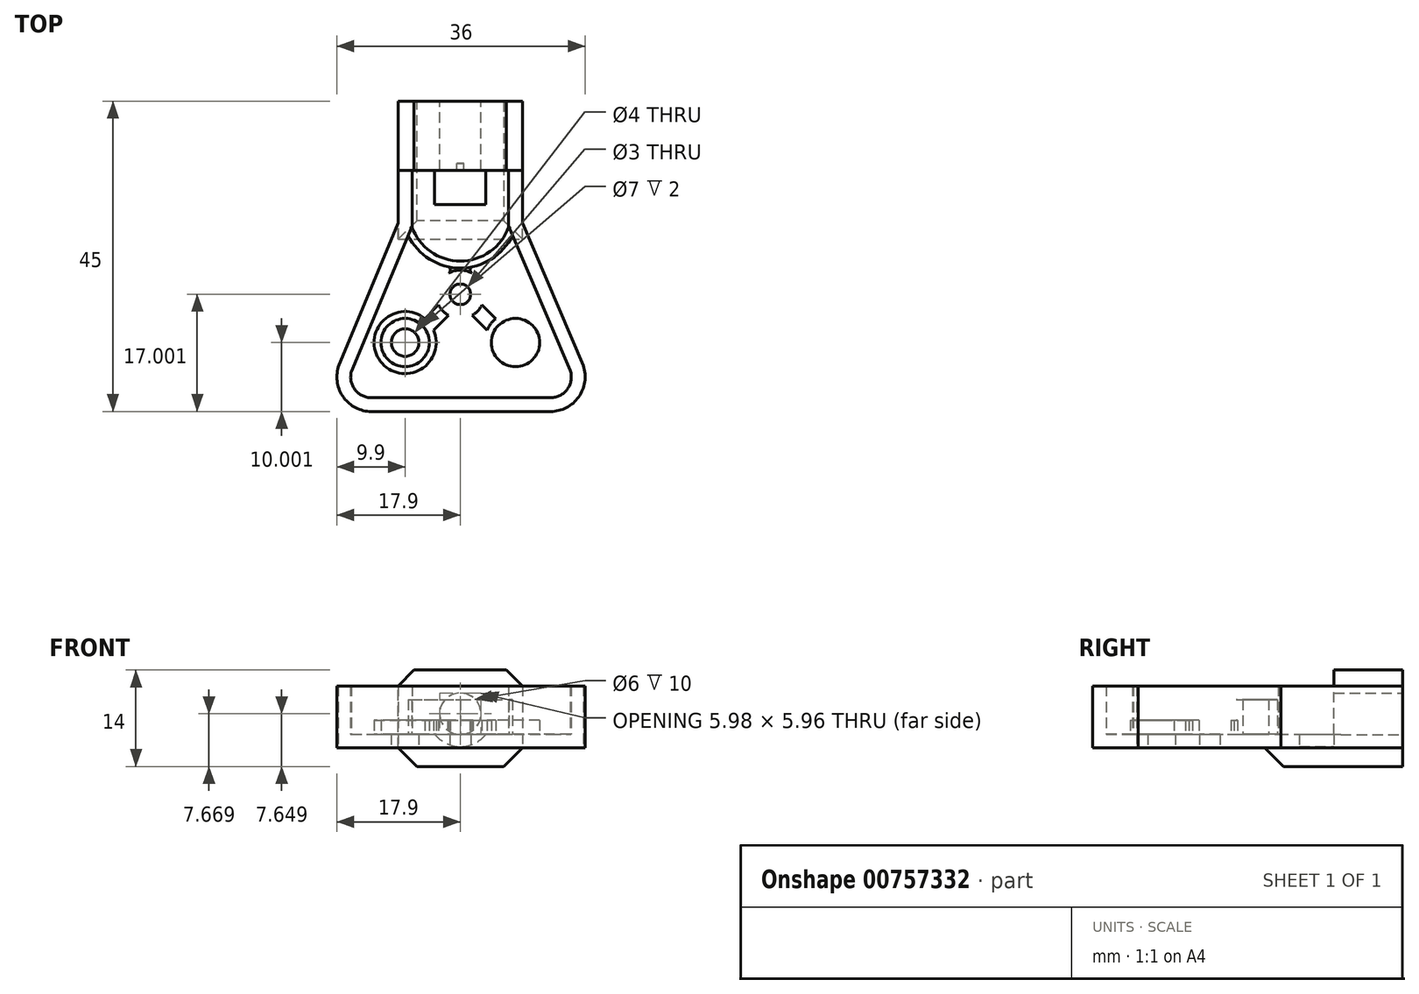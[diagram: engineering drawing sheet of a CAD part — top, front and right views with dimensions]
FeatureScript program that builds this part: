
annotation { "Feature Type Name" : "Feature", "Feature Type Description" : "" }
export const myFeature = defineFeature(function(context is Context, id is Id, definition is map)
    precondition{}
    {
        {
            var Q0;
            Q0=qCreatedBy(makeId("Top.planeOp"),FACE);
            var sketch = newSketch(context, id + "F0", { "sketchPlane" : qUnion([Q0])});
            skLineSegment(sketch, "E0", {"start": v(0, 29.44) * mm, "end": v(0, -20.56) * mm, "construction": true});
            skLineSegment(sketch, "E1", {"start": v(0, 29.44) * mm, "end": v(-9, 29.44) * mm});
            skLineSegment(sketch, "E2", {"start": v(0, 29.44) * mm, "end": v(9, 29.44) * mm});
            skLineSegment(sketch, "E3", {"start": v(10, 4.44) * mm, "end": v(10, 4.42) * mm, "construction": true});
            skLineSegment(sketch, "E4", {"start": v(-10, 4.44) * mm, "end": v(-10, 4.37) * mm, "construction": true});
            skCircle(sketch, "E5", {"center": v(-8, -10.56) * mm, "radius": 2 * mm});
            skCircle(sketch, "E6", {"center": v(8, -10.56) * mm, "radius": 2 * mm});
            skCircle(sketch, "E7", {"center": v(0, -3.56) * mm, "radius": 1.5 * mm});
            skArc(sketch, "E8", {"start": v(13.1, -20.56) * mm, "mid": v(17.17, -18.46) * mm, "end": v(17.82, -13.92) * mm});
            skLineSegment(sketch, "E9", {"start": v(-12.9, -20.56) * mm, "end": v(13.1, -20.56) * mm});
            skLineSegment(sketch, "E10", {"start": v(10, 4.44) * mm, "end": v(10, 4.44) * mm, "construction": true});
            skLineSegment(sketch, "E11", {"start": v(-17.7, -14.12) * mm, "end": v(-9, 6.77) * mm});
            skLineSegment(sketch, "E12", {"start": v(-9, 6.77) * mm, "end": v(-9, 15.44) * mm});
            skArc(sketch, "E13", {"start": v(-17.7, -14.12) * mm, "mid": v(-16.92, -18.54) * mm, "end": v(-12.9, -20.56) * mm});
            skLineSegment(sketch, "E14", {"start": v(17.82, -13.92) * mm, "end": v(9, 6.77) * mm});
            skLineSegment(sketch, "E15", {"start": v(9, 6.77) * mm, "end": v(9, 15.44) * mm});
            skLineSegment(sketch, "E16.trimOffspring", {"start": v(-9.97, 4.44) * mm, "end": v(-10, 4.44) * mm, "construction": true});
            skLineSegment(sketch, "E17.trimOffspring", {"start": v(-1.5, -3.56) * mm, "end": v(0, -3.56) * mm, "construction": true});
            skArc(sketch, "E18.0", {"start": v(-15.8, -14.78) * mm, "mid": v(-15.28, -17.38) * mm, "end": v(-12.9, -18.56) * mm});
            skLineSegment(sketch, "E19.0", {"start": v(-15.8, -14.78) * mm, "end": v(-7, 6.37) * mm});
            skLineSegment(sketch, "E20.0", {"start": v(15.95, -14.63) * mm, "end": v(7, 6.36) * mm});
            skArc(sketch, "E21.0", {"start": v(13.1, -18.56) * mm, "mid": v(15.52, -17.32) * mm, "end": v(15.95, -14.63) * mm});
            skLineSegment(sketch, "E22.0", {"start": v(-12.9, -18.56) * mm, "end": v(13.1, -18.56) * mm});
            skLineSegment(sketch, "E23.0", {"start": v(-7, 6.34) * mm, "end": v(-7, 15.44) * mm});
            skLineSegment(sketch, "E24.0", {"start": v(7, 6.34) * mm, "end": v(7, 15.44) * mm});
            skLineSegment(sketch, "E25", {"start": v(-9, 15.44) * mm, "end": v(9, 15.44) * mm});
            skPoint(sketch, "E26.end.orphan", {"position": v(-2.9, 15.44) * mm});
            skLineSegment(sketch, "E27", {"start": v(-9, 15.44) * mm, "end": v(-9, 29.44) * mm});
            skLineSegment(sketch, "E28", {"start": v(9, 15.44) * mm, "end": v(9, 29.44) * mm});
            skSolve(sketch);
        }
        {
            var Q0;
            Q0=makeQuery(id+"F0.imprint","IMPRINT",FACE,{"disambiguationData":[TD([[makeQuery(id+"F0.imprint","IMPRINT",EDGE,{"derivedFrom":sQuery(id+"F0.wireOp",EDGE,"E5")}),-1.0]])]});
            extrude(context, id + "F1", {"entities" : qUnion([Q0]), "depth" : 2 * mm, "offsetDistance" : 25 * mm});
        }
        {
            var Q0;
            Q0=makeQuery(id+"F0.imprint","IMPRINT",FACE,{"disambiguationData":[TD([[makeQuery(id+"F0.imprint","IMPRINT",EDGE,{"derivedFrom":sQuery(id+"F0.wireOp",EDGE,"E8")}),1.0]])]});
            extrude(context, id + "F2", {"entities" : qUnion([Q0]), "operationType" : NewBodyOperationType.ADD, "depth" : 9 * mm, "offsetDistance" : 25 * mm});
        }
        {
            var Q0;
            Q0=qCreatedBy(makeId("Front.planeOp"),FACE);
            cPlane(context, id + "F3", {"entities" : qUnion([Q0]), "cplaneType" : CPlaneType.OFFSET, "offset" : 29.44 * mm, "oppositeDirection" : true, "width" : 150 * mm, "height" : 150 * mm});
        }
        {
            var Q0;
            Q0=qCreatedBy(makeId("Top.planeOp"),FACE);
            var sketch = newSketch(context, id + "F4", { "sketchPlane" : qUnion([Q0])});
            skCircle(sketch, "E29.0", {"center": v(-8, -10.56) * mm, "radius": 3.5 * mm});
            skCircle(sketch, "E30.0", {"center": v(-8, -10.56) * mm, "radius": 4.5 * mm});
            skCircle(sketch, "E31.0", {"center": v(0, -3.56) * mm, "radius": 2.5 * mm});
            skCircle(sketch, "E32.0", {"center": v(0, -3.56) * mm, "radius": 3.5 * mm});
            skLineSegment(sketch, "E33", {"start": v(-3.15, -5.09) * mm, "end": v(-5.14, -7.08) * mm});
            skLineSegment(sketch, "E34", {"start": v(-1.73, -6.6) * mm, "end": v(-3.88, -8.75) * mm});
            skArc(sketch, "E35", {"start": v(-7.05, 6.31) * mm, "mid": v(-4.33, 2.66) * mm, "end": v(0, 1.25) * mm});
            skArc(sketch, "E36.0", {"start": v(-8, 5.98) * mm, "mid": v(-4.91, 1.84) * mm, "end": v(0, 0.25) * mm});
            skArc(sketch, "E37", {"start": v(-1.64, -0.47) * mm, "mid": v(-1.44, 0.05) * mm, "end": v(-1.82, 0.46) * mm});
            skCircle(sketch, "E38.MirrorC", {"center": v(8, -10.56) * mm, "radius": 3.5 * mm});
            skCircle(sketch, "E39.MirrorC", {"center": v(8, -10.56) * mm, "radius": 4.5 * mm});
            skArc(sketch, "E40.MirrorCS", {"start": v(1.64, -0.47) * mm, "mid": v(1.44, 0.05) * mm, "end": v(1.82, 0.46) * mm});
            skArc(sketch, "E41.MirrorCS", {"start": v(8, 5.98) * mm, "mid": v(4.91, 1.84) * mm, "end": v(0, 0.25) * mm});
            skLineSegment(sketch, "E42.MirrorCS", {"start": v(1.73, -6.6) * mm, "end": v(3.88, -8.75) * mm});
            skLineSegment(sketch, "E43.MirrorCS", {"start": v(3.15, -5.09) * mm, "end": v(5.14, -7.08) * mm});
            skArc(sketch, "E44.MirrorCS", {"start": v(7.05, 6.31) * mm, "mid": v(4.33, 2.66) * mm, "end": v(0, 1.25) * mm});
            skPoint(sketch, "E45.orphan", {"position": v(-8.1, 6.09) * mm});
            skPoint(sketch, "E46.orphan", {"position": v(-7.16, 6.4) * mm});
            skPoint(sketch, "E47.orphan", {"position": v(8.1, 6.09) * mm});
            skPoint(sketch, "E48.orphan", {"position": v(7.16, 6.4) * mm});
            skLineSegment(sketch, "E49", {"start": v(8, 5.98) * mm, "end": v(7.05, 6.31) * mm});
            skLineSegment(sketch, "E50", {"start": v(-8, 5.98) * mm, "end": v(-7.05, 6.31) * mm});
            skSolve(sketch);
        }
        {
            var Q0;
            Q0=makeQuery(id+"F4.imprint","IMPRINT",FACE,{"disambiguationData":[TD([[makeQuery(id+"F4.imprint","IMPRINT",EDGE,{"derivedFrom":sQuery(id+"F4.wireOp",EDGE,"E35")}),-1.0]])]});
            var Q1;
            Q1=sQuery(id+"F4.wireOp",EDGE,"E36.0");
            var Q2;
            Q2=sQuery(id+"F4.wireOp",EDGE,"E41.MirrorCS");
            var Q3;
            Q3=sQuery(id+"F4.wireOp",EDGE,"E49");
            var Q4;
            Q4=sQuery(id+"F4.wireOp",EDGE,"E44.MirrorCS");
            var Q5;
            Q5=sQuery(id+"F4.wireOp",EDGE,"E35");
            var Q6;
            Q6=sQuery(id+"F4.wireOp",EDGE,"E50");
            extrude(context, id + "F5", {"entities" : qUnion([Q0]), "surfaceOperationType" : NewSurfaceOperationType.ADD, "surfaceEntities" : qUnion([Q1, Q2, Q3, Q4, Q5, Q6]), "depth" : 7 * mm, "offsetDistance" : 25 * mm});
        }
        {
            var Q0;
            Q0=makeQuery(id+"F4.imprint","IMPRINT",FACE,{"disambiguationData":[TD([[makeQuery(id+"F4.imprint","IMPRINT",EDGE,{"derivedFrom":sQuery(id+"F4.wireOp",EDGE,"E29.0")}),-1.0]])]});
            var Q1;
            {var subQ0=sQuery(id+"F4.wireOp",EDGE,"E33");Q1=makeQuery(id+"F4.imprint","IMPRINT",FACE,{"disambiguationData":[TD([[makeQuery(id+"F4.imprint","IMPRINT",EDGE,{"derivedFrom":subQ0}),1.0]])]});}
            var Q2;
            Q2=makeQuery(id+"F4.imprint","IMPRINT",FACE,{"disambiguationData":[TD([[makeQuery(id+"F4.imprint","IMPRINT",EDGE,{"derivedFrom":sQuery(id+"F4.wireOp",EDGE,"E31.0")}),1.0]])]});
            var Q3;
            {var subQ0=sQuery(id+"F4.wireOp",EDGE,"E42.MirrorCS");Q3=makeQuery(id+"F4.imprint","IMPRINT",FACE,{"disambiguationData":[TD([[makeQuery(id+"F4.imprint","IMPRINT",EDGE,{"derivedFrom":subQ0}),1.0]])]});}
            var Q4;
            Q4=makeQuery(id+"F4.imprint","IMPRINT",FACE,{"disambiguationData":[TD([[makeQuery(id+"F4.imprint","IMPRINT",EDGE,{"derivedFrom":sQuery(id+"F4.wireOp",EDGE,"E38.MirrorC")}),1.0]])]});
            var Q5;
            {var subQ4=sQuery(id+"F4.wireOp",EDGE,"E37");Q5=makeQuery(id+"F4.imprint","IMPRINT",FACE,{"disambiguationData":[TD([[makeQuery(id+"F4.imprint","IMPRINT",EDGE,{"derivedFrom":subQ4}),-1.0]])]});}
            extrude(context, id + "F6", {"entities" : qUnion([Q0, Q1, Q2, Q3, Q4, Q5]), "operationType" : NewBodyOperationType.ADD, "depth" : 4 * mm, "offsetDistance" : 25 * mm});
        }
        {
            var Q0;
            Q0=qCreatedBy(id+"F3.planeOp",FACE);
            cPlane(context, id + "F7", {"entities" : qUnion([Q0]), "cplaneType" : CPlaneType.OFFSET, "offset" : 5 * mm, "width" : 150 * mm, "height" : 150 * mm});
        }
        {
            var Q0;
            Q0=qCreatedBy(id+"F7.planeOp",FACE);
            var sketch = newSketch(context, id + "F8", { "sketchPlane" : qUnion([Q0])});
            skLineSegment(sketch, "E51", {"start": v(9, 9.66) * mm, "end": v(9, 2.66) * mm, "construction": true});
            skLineSegment(sketch, "E52", {"start": v(9, 6.16) * mm, "end": v(-9, 6.16) * mm, "construction": true});
            skCircle(sketch, "E53", {"center": v(0, 4.96) * mm, "radius": 3 * mm});
            skLineSegment(sketch, "E54", {"start": v(-9, -2.69) * mm, "end": v(-9, 11.31) * mm});
            skLineSegment(sketch, "E55", {"start": v(-9, 11.31) * mm, "end": v(9, 11.31) * mm});
            skLineSegment(sketch, "E56", {"start": v(9, 11.31) * mm, "end": v(9, -2.69) * mm});
            skLineSegment(sketch, "E57", {"start": v(9, -2.69) * mm, "end": v(-9, -2.69) * mm});
            skSolve(sketch);
        }
        {
            var Q0;
            Q0 = qSketchRegion(id + "F8", true);
            extrude(context, id + "F9", {"entities" : qUnion([Q0]), "operationType" : NewBodyOperationType.ADD, "depth" : 10 * mm, "offsetDistance" : 25 * mm});
        }
        {
            var Q0;
            Q0=qCreatedBy(id+"F7.planeOp",FACE);
            cPlane(context, id + "F10", {"entities" : qUnion([Q0]), "cplaneType" : CPlaneType.OFFSET, "offset" : 10 * mm, "width" : 150 * mm, "height" : 150 * mm});
        }
        {
            var Q0;
            Q0=qCreatedBy(id+"F10.planeOp",FACE);
            var sketch = newSketch(context, id + "F11", { "sketchPlane" : qUnion([Q0])});
            skCircle(sketch, "E58", {"center": v(0, 4.96) * mm, "radius": 4.75 * mm});
            skSolve(sketch);
        }
        {
            var Q0;
            Q0=makeQuery(id+"F11.imprint","IMPRINT",FACE,{"disambiguationData":[TD([[makeQuery(id+"F11.imprint","IMPRINT",EDGE,{"derivedFrom":sQuery(id+"F11.wireOp",EDGE,"E58")}),1.0]])]});
            extrude(context, id + "F12", {"entities" : qUnion([Q0]), "operationType" : NewBodyOperationType.REMOVE, "depth" : 5 * mm, "offsetDistance" : 25 * mm});
        }
        {
            var Q0;
            {var subQ10=sQuery(id+"F8.wireOp",EDGE,"E56");var subQ11=sQuery(id+"F8.wireOp",EDGE,"E54");var subQ12=sQuery(id+"F8.wireOp",EDGE,"E57");Q0=makeQuery(id+"F9.boolean.opBoolean","SPLIT",FACE,{"disambiguationData":[TD([makeQuery(id+"F9.opExtrude","SWEPT_FACE",FACE,{"disambiguationData":[OSD([subQ12])]})])],"derivedFrom":makeQuery(id+"F9.opExtrude","CAP_FACE",FACE,{"disambiguationData":[OSD([sQuery(id+"F8.wireOp",EDGE,"E53"),subQ11,sQuery(id+"F8.wireOp",EDGE,"E55"),subQ10,subQ12])],"isStart":false})});}
            extrude(context, id + "F13", {"entities" : qUnion([Q0]), "operationType" : NewBodyOperationType.ADD, "depth" : 10 * mm, "offsetDistance" : 25 * mm});
        }
        {
            var Q0;
            Q0=makeQuery(id+"F13.opExtrude","CAP_EDGE",EDGE,{"disambiguationData":[OSD([sQuery(id+"F8.wireOp",EDGE,"E57")])],"isStart":false});
            chamfer(context, id + "F14", {"entities" : qUnion([Q0]), "width" : 2.69 * mm, "tangentPropagation" : true});
        }
        {
            var Q0;
            Q0=makeQuery(id+"F9.opExtrude","SWEPT_EDGE",EDGE,{"disambiguationData":[OSD([sQuery(id+"F8.wireOp",EDGE,"E54"),sQuery(id+"F8.wireOp",EDGE,"E55")])]});
            var Q1;
            Q1=makeQuery(id+"F9.opExtrude","SWEPT_EDGE",EDGE,{"disambiguationData":[OSD([sQuery(id+"F8.wireOp",EDGE,"E55"),sQuery(id+"F8.wireOp",EDGE,"E56")])]});
            chamfer(context, id + "F15", {"entities" : qUnion([Q0, Q1]), "width" : 2.3 * mm, "tangentPropagation" : true});
        }
        {
            var Q0;
            {var subQ0=sQuery(id+"F8.wireOp",EDGE,"E57");var subQ1=sQuery(id+"F8.wireOp",EDGE,"E56");Q0=makeQuery(id+"F13.boolean.opBoolean","MERGE",EDGE,{"derivedFrom":[makeQuery(id+"F9.opExtrude","SWEPT_EDGE",EDGE,{"disambiguationData":[OSD([subQ1,subQ0])]}),makeQuery(id+"F13.opExtrude","SWEPT_EDGE",EDGE,{"disambiguationData":[OSD([subQ1,subQ0])]})]});}
            var Q1;
            {var subQ0=sQuery(id+"F8.wireOp",EDGE,"E57");var subQ1=sQuery(id+"F8.wireOp",EDGE,"E54");Q1=makeQuery(id+"F13.boolean.opBoolean","MERGE",EDGE,{"derivedFrom":[makeQuery(id+"F9.opExtrude","SWEPT_EDGE",EDGE,{"disambiguationData":[OSD([subQ1,subQ0])]}),makeQuery(id+"F13.opExtrude","SWEPT_EDGE",EDGE,{"disambiguationData":[OSD([subQ1,subQ0])]})]});}
            chamfer(context, id + "F16", {"entities" : qUnion([Q0, Q1]), "width" : 2.69 * mm, "tangentPropagation" : true});
        }
    });
